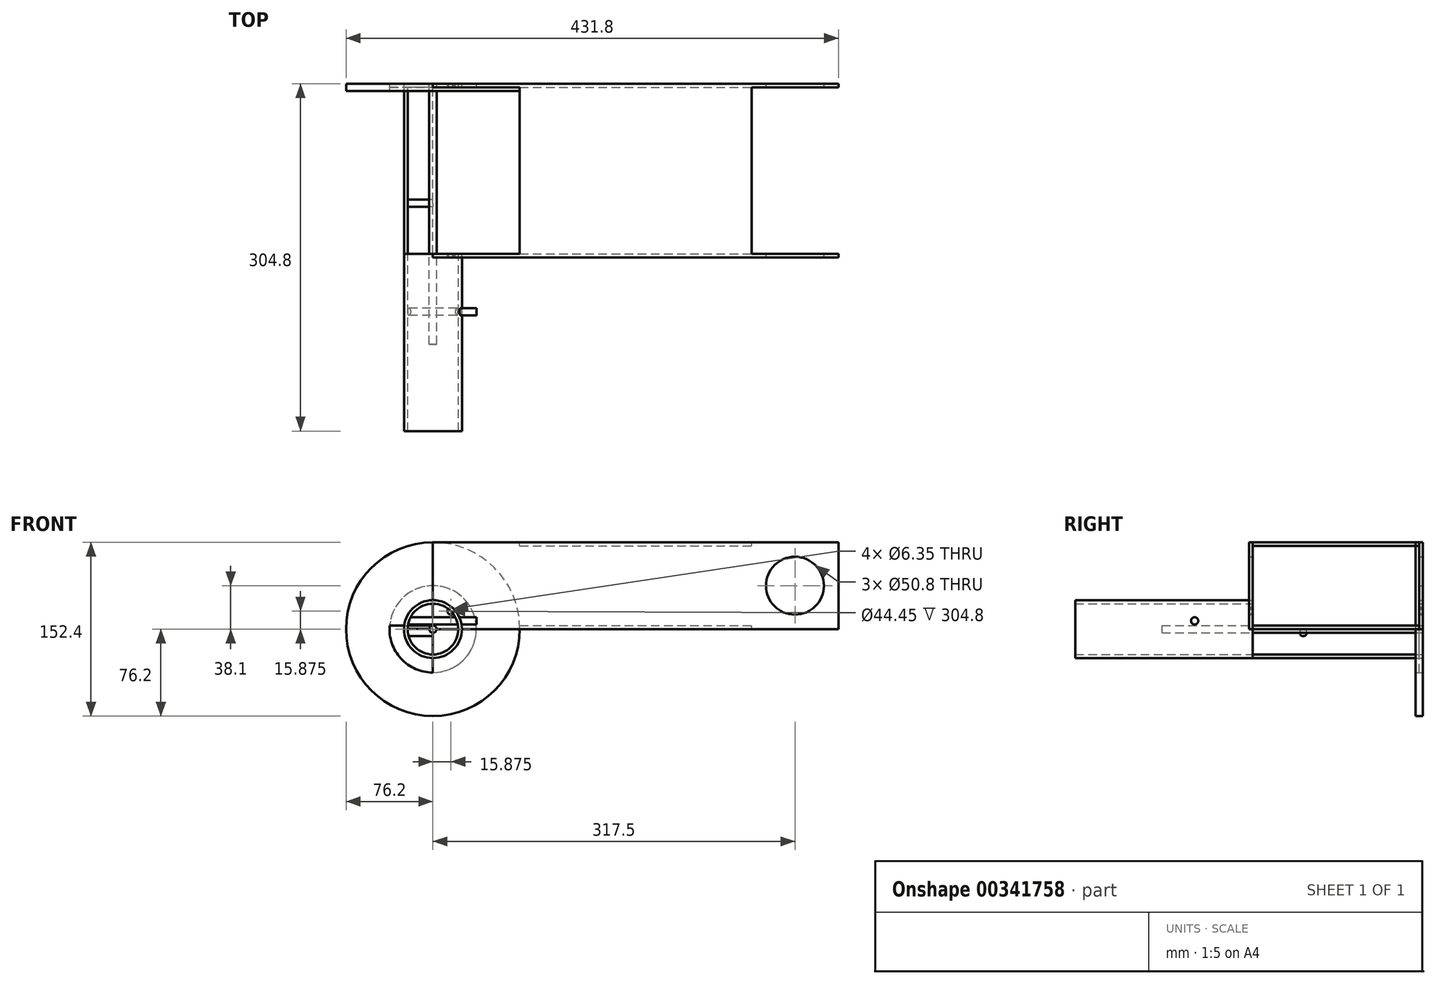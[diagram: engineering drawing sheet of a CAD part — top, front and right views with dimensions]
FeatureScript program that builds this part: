
annotation { "Feature Type Name" : "Feature", "Feature Type Description" : "" }
export const myFeature = defineFeature(function(context is Context, id is Id, definition is map)
    precondition{}
    {
        {
            var Q0;
            Q0=qCreatedBy(makeId("Front.planeOp"),FACE);
            var sketch = newSketch(context, id + "F0", { "sketchPlane" : qUnion([Q0])});
            skCircle(sketch, "E0", {"center": v(0, 0) * mm, "radius": 38.1 * mm});
            skCircle(sketch, "E1", {"center": v(0, 0) * mm, "radius": 3.18 * mm});
            skSolve(sketch);
        }
        {
            var Q0;
            Q0 = qSketchRegion(id + "F0", true);
            extrude(context, id + "F1", {"entities" : qUnion([Q0]), "depth" : 6.35 * mm});
        }
        {
            var Q0;
            Q0=qCreatedBy(makeId("Front.planeOp"),FACE);
            var sketch = newSketch(context, id + "F2", { "sketchPlane" : qUnion([Q0])});
            skCircle(sketch, "E2", {"center": v(0, 0) * mm, "radius": 25.4 * mm});
            skCircle(sketch, "E3", {"center": v(0, 0) * mm, "radius": 22.23 * mm});
            skSolve(sketch);
        }
        {
            var Q0;
            Q0 = qSketchRegion(id + "F2", true);
            extrude(context, id + "F3", {"entities" : qUnion([Q0]), "depth" : 304.8 * mm});
        }
        {
            var Q0;
            Q0=qCreatedBy(makeId("Right.planeOp"),FACE);
            var sketch = newSketch(context, id + "F4", { "sketchPlane" : qUnion([Q0])});
            skCircle(sketch, "E4", {"center": v(-200.03, 7.27) * mm, "radius": 3.18 * mm});
            skCircle(sketch, "E5", {"center": v(-104.78, -3.04) * mm, "radius": 3.18 * mm});
            skSolve(sketch);
        }
        {
            var Q0;
            Q0 = qSketchRegion(id + "F4", true);
            var Q1;
            Q1=makeQuery(id+"F3.opExtrude","SWEPT_FACE",FACE,{"disambiguationData":[OSD([sQuery(id+"F2.wireOp",EDGE,"E3")])]});
            extrude(context, id + "F5", {"entities" : qUnion([Q0]), "operationType" : NewBodyOperationType.ADD, "depth" : 38.1 * mm, "hasSecondDirection" : true, "secondDirectionBound" : SecondDirectionBoundingType.UP_TO_SURFACE, "secondDirectionOppositeDirection" : true, "secondDirectionBoundEntityFace" : qUnion([Q1]), "secondDirectionDepth" : 25.4 * mm});
        }
        {
            var Q0;
            Q0=qCreatedBy(makeId("Front.planeOp"),FACE);
            var sketch = newSketch(context, id + "F6", { "sketchPlane" : qUnion([Q0])});
            skLineSegment(sketch, "E6.bottom", {"start": v(0, 0) * mm, "end": v(355.6, 0) * mm});
            skLineSegment(sketch, "E6.top", {"start": v(0, 76.2) * mm, "end": v(355.6, 76.2) * mm});
            skLineSegment(sketch, "E6.left", {"start": v(0, 0) * mm, "end": v(0, 76.2) * mm});
            skLineSegment(sketch, "E6.right", {"start": v(355.6, 0) * mm, "end": v(355.6, 76.2) * mm});
            skSolve(sketch);
        }
        {
            var Q0;
            Q0 = qSketchRegion(id + "F6", true);
            extrude(context, id + "F7", {"entities" : qUnion([Q0]), "depth" : 152.4 * mm});
        }
        {
            var Q0;
            Q0=makeQuery(id+"F7.opExtrude","SWEPT_FACE",FACE,{"disambiguationData":[OSD([sQuery(id+"F6.wireOp",EDGE,"E6.top")])]});
            var sketch = newSketch(context, id + "F8", { "sketchPlane" : qUnion([Q0])});
            skLineSegment(sketch, "E7.bottom", {"start": v(0, -3.18) * mm, "end": v(76.2, -3.18) * mm});
            skLineSegment(sketch, "E7.top", {"start": v(0, -149.22) * mm, "end": v(76.2, -149.22) * mm});
            skLineSegment(sketch, "E7.left", {"start": v(0, -3.18) * mm, "end": v(0, -149.22) * mm});
            skLineSegment(sketch, "E7.right", {"start": v(76.2, -3.18) * mm, "end": v(76.2, -149.23) * mm});
            skLineSegment(sketch, "E8.bottom", {"start": v(355.6, -3.17) * mm, "end": v(279.4, -3.17) * mm});
            skLineSegment(sketch, "E8.top", {"start": v(355.6, -149.22) * mm, "end": v(279.4, -149.22) * mm});
            skLineSegment(sketch, "E8.left", {"start": v(355.6, -3.17) * mm, "end": v(355.6, -149.22) * mm});
            skLineSegment(sketch, "E8.right", {"start": v(279.4, -3.17) * mm, "end": v(279.4, -149.22) * mm});
            skSolve(sketch);
        }
        {
            var Q0;
            Q0 = qSketchRegion(id + "F8", true);
            extrude(context, id + "F9", {"entities" : qUnion([Q0]), "operationType" : NewBodyOperationType.REMOVE, "endBound" : BoundingType.THROUGH_ALL, "oppositeDirection" : true, "depth" : 25.4 * mm});
        }
        {
            var Q0;
            Q0=makeQuery(id+"F9.boolean.opBoolean","COPY",FACE,{"derivedFrom":makeQuery(id+"F9.opExtrude","SWEPT_FACE",FACE,{"disambiguationData":[OSD([sQuery(id+"F8.wireOp",EDGE,"E8.right")])]})});
            var sketch = newSketch(context, id + "F10", { "sketchPlane" : qUnion([Q0])});
            skLineSegment(sketch, "E9.bottom", {"start": v(-3.18, 73.03) * mm, "end": v(-149.23, 73.03) * mm});
            skLineSegment(sketch, "E9.top", {"start": v(-3.18, 3.18) * mm, "end": v(-149.23, 3.17) * mm});
            skLineSegment(sketch, "E9.left", {"start": v(-3.18, 73.03) * mm, "end": v(-3.18, 3.18) * mm});
            skLineSegment(sketch, "E9.right", {"start": v(-149.23, 73.03) * mm, "end": v(-149.23, 3.17) * mm});
            skSolve(sketch);
        }
        {
            var Q0;
            Q0 = qSketchRegion(id + "F10", true);
            extrude(context, id + "F11", {"entities" : qUnion([Q0]), "operationType" : NewBodyOperationType.REMOVE, "endBound" : BoundingType.THROUGH_ALL, "oppositeDirection" : true, "depth" : 25.4 * mm});
        }
        {
            var Q0;
            Q0=makeQuery(id+"F7.opExtrude","CAP_FACE",FACE,{"disambiguationData":[OSD([sQuery(id+"F6.wireOp",EDGE,"E6.bottom"),sQuery(id+"F6.wireOp",EDGE,"E6.top"),sQuery(id+"F6.wireOp",EDGE,"E6.left"),sQuery(id+"F6.wireOp",EDGE,"E6.right")])],"isStart":true});
            var sketch = newSketch(context, id + "F12", { "sketchPlane" : qUnion([Q0])});
            skCircle(sketch, "E10", {"center": v(-317.5, 38.1) * mm, "radius": 25.4 * mm});
            skSolve(sketch);
        }
        {
            var Q0;
            Q0 = qSketchRegion(id + "F12", true);
            extrude(context, id + "F13", {"entities" : qUnion([Q0]), "operationType" : NewBodyOperationType.REMOVE, "endBound" : BoundingType.THROUGH_ALL, "oppositeDirection" : true, "depth" : 25.4 * mm});
        }
        {
            var Q0;
            Q0=makeQuery(id+"F7.opExtrude","CAP_FACE",FACE,{"disambiguationData":[OSD([sQuery(id+"F6.wireOp",EDGE,"E6.bottom"),sQuery(id+"F6.wireOp",EDGE,"E6.top"),sQuery(id+"F6.wireOp",EDGE,"E6.left"),sQuery(id+"F6.wireOp",EDGE,"E6.right")])],"isStart":false});
            var sketch = newSketch(context, id + "F14", { "sketchPlane" : qUnion([Q0])});
            skCircle(sketch, "E11", {"center": v(15.87, 15.88) * mm, "radius": 3.18 * mm});
            skSolve(sketch);
        }
        {
            var Q0;
            Q0 = qSketchRegion(id + "F14", true);
            extrude(context, id + "F15", {"entities" : qUnion([Q0]), "operationType" : NewBodyOperationType.REMOVE, "endBound" : BoundingType.THROUGH_ALL, "oppositeDirection" : true, "depth" : 25.4 * mm});
        }
        {
            var Q0;
            Q0=qCreatedBy(makeId("Front.planeOp"),FACE);
            var sketch = newSketch(context, id + "F16", { "sketchPlane" : qUnion([Q0])});
            skCircle(sketch, "E12", {"center": v(0, 0) * mm, "radius": 25.4 * mm});
            skCircle(sketch, "E13", {"center": v(0, 0) * mm, "radius": 76.2 * mm});
            skSolve(sketch);
        }
        {
            var Q0;
            Q0 = qSketchRegion(id + "F16", true);
            extrude(context, id + "F17", {"entities" : qUnion([Q0]), "depth" : 6.35 * mm});
        }
        {
            var Q0;
            Q0=qCreatedBy(makeId("Front.planeOp"),FACE);
            var sketch = newSketch(context, id + "F18", { "sketchPlane" : qUnion([Q0])});
            skCircle(sketch, "E14", {"center": v(0, 0) * mm, "radius": 3.18 * mm});
            skSolve(sketch);
        }
        {
            var Q0;
            Q0 = qSketchRegion(id + "F18", true);
            extrude(context, id + "F19", {"entities" : qUnion([Q0]), "depth" : 228.6 * mm});
        }
    });
